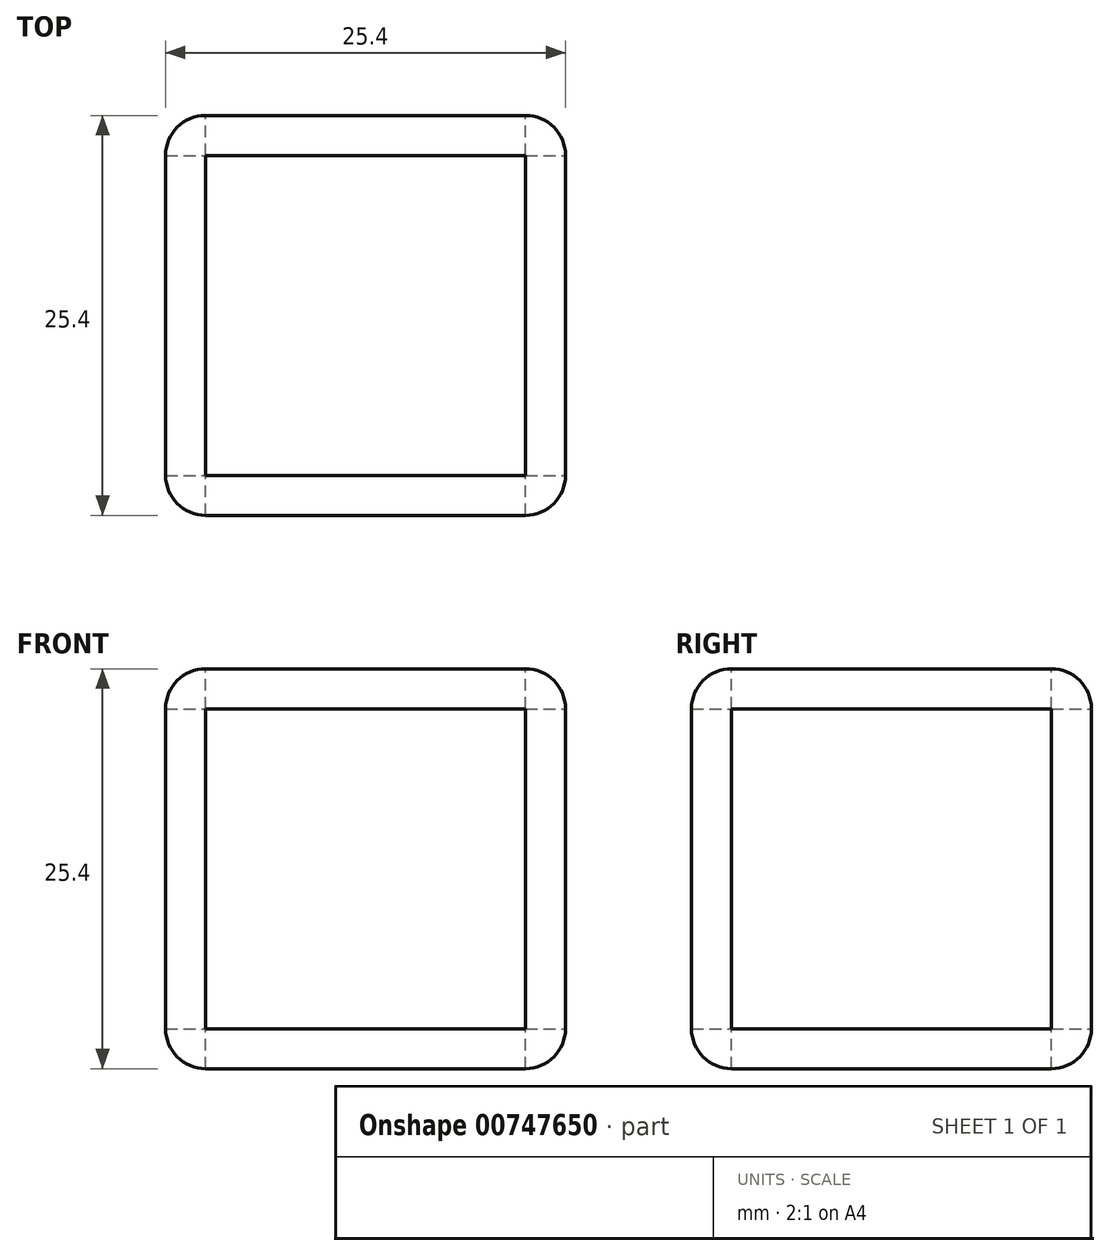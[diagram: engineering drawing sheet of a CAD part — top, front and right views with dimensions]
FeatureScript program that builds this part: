
annotation { "Feature Type Name" : "Feature", "Feature Type Description" : "" }
export const myFeature = defineFeature(function(context is Context, id is Id, definition is map)
    precondition{}
    {
        {
            var Q0;
            Q0=qCreatedBy(makeId("Front.planeOp"),FACE);
            var sketch = newSketch(context, id + "F0", { "sketchPlane" : qUnion([Q0])});
            skLineSegment(sketch, "E0.bottom", {"start": v(0, 0) * mm, "end": v(25.4, 0) * mm});
            skLineSegment(sketch, "E0.top", {"start": v(0, -25.4) * mm, "end": v(25.4, -25.4) * mm});
            skLineSegment(sketch, "E0.left", {"start": v(0, 0) * mm, "end": v(0, -25.4) * mm});
            skLineSegment(sketch, "E0.right", {"start": v(25.4, 0) * mm, "end": v(25.4, -25.4) * mm});
            skSolve(sketch);
        }
        {
            var Q0;
            Q0 = qSketchRegion(id + "F0", true);
            extrude(context, id + "F1", {"entities" : qUnion([Q0]), "depth" : 25.4 * mm, "offsetDistance" : 25.4 * mm});
        }
        {
            var Q0;
            Q0=makeQuery(id+"F1.opExtrude","CAP_EDGE",EDGE,{"disambiguationData":[OSD([sQuery(id+"F0.wireOp",EDGE,"E0.left")])],"isStart":true});
            var Q1;
            Q1=makeQuery(id+"F1.opExtrude","CAP_EDGE",EDGE,{"disambiguationData":[OSD([sQuery(id+"F0.wireOp",EDGE,"E0.left")])],"isStart":false});
            var Q2;
            Q2=makeQuery(id+"F1.opExtrude","SWEPT_EDGE",EDGE,{"disambiguationData":[OSD([sQuery(id+"F0.wireOp",EDGE,"E0.top"),sQuery(id+"F0.wireOp",EDGE,"E0.left")])]});
            var Q3;
            Q3=makeQuery(id+"F1.opExtrude","CAP_EDGE",EDGE,{"disambiguationData":[OSD([sQuery(id+"F0.wireOp",EDGE,"E0.top")])],"isStart":true});
            var Q4;
            Q4=makeQuery(id+"F1.opExtrude","CAP_EDGE",EDGE,{"disambiguationData":[OSD([sQuery(id+"F0.wireOp",EDGE,"E0.right")])],"isStart":true});
            var Q5;
            Q5=makeQuery(id+"F1.opExtrude","CAP_EDGE",EDGE,{"disambiguationData":[OSD([sQuery(id+"F0.wireOp",EDGE,"E0.bottom")])],"isStart":true});
            var Q6;
            Q6=makeQuery(id+"F1.opExtrude","SWEPT_EDGE",EDGE,{"disambiguationData":[OSD([sQuery(id+"F0.wireOp",EDGE,"E0.bottom"),sQuery(id+"F0.wireOp",EDGE,"E0.left")])]});
            var Q7;
            Q7=makeQuery(id+"F1.opExtrude","SWEPT_EDGE",EDGE,{"disambiguationData":[OSD([sQuery(id+"F0.wireOp",EDGE,"E0.bottom"),sQuery(id+"F0.wireOp",EDGE,"E0.right")])]});
            var Q8;
            Q8=makeQuery(id+"F1.opExtrude","SWEPT_EDGE",EDGE,{"disambiguationData":[OSD([sQuery(id+"F0.wireOp",EDGE,"E0.top"),sQuery(id+"F0.wireOp",EDGE,"E0.right")])]});
            var Q9;
            Q9=makeQuery(id+"F1.opExtrude","CAP_EDGE",EDGE,{"disambiguationData":[OSD([sQuery(id+"F0.wireOp",EDGE,"E0.right")])],"isStart":false});
            var Q10;
            Q10=makeQuery(id+"F1.opExtrude","CAP_EDGE",EDGE,{"disambiguationData":[OSD([sQuery(id+"F0.wireOp",EDGE,"E0.bottom")])],"isStart":false});
            fillet(context, id + "F2", {"entities" : qUnion([Q0, Q1, Q2, Q3, Q4, Q5, Q6, Q7, Q8, Q9, Q10]), "radius" : 2.54 * mm, "tangentPropagation" : true, "allowEdgeOverflow" : false});
        }
        {
            var Q0;
            Q0=makeQuery(id+"F1.opExtrude","CAP_EDGE",EDGE,{"disambiguationData":[OSD([sQuery(id+"F0.wireOp",EDGE,"E0.top")])],"isStart":false});
            fillet(context, id + "F3", {"entities" : qUnion([Q0]), "radius" : 2.54 * mm, "tangentPropagation" : true, "allowEdgeOverflow" : false});
        }
        {
            var Q0;
            Q0=makeQuery(id+"F1.opExtrude","SWEPT_FACE",FACE,{"disambiguationData":[OSD([sQuery(id+"F0.wireOp",EDGE,"E0.bottom")])]});
            extrude(context, id + "F4", {"entities" : qUnion([Q0]), "operationType" : NewBodyOperationType.REMOVE, "endBound" : BoundingType.THROUGH_ALL, "oppositeDirection" : true, "depth" : 25.4 * mm, "offsetDistance" : 25.4 * mm});
        }
        {
            var Q0;
            Q0=makeQuery(id+"F1.opExtrude","SWEPT_FACE",FACE,{"disambiguationData":[OSD([sQuery(id+"F0.wireOp",EDGE,"E0.right")])]});
            extrude(context, id + "F5", {"entities" : qUnion([Q0]), "operationType" : NewBodyOperationType.REMOVE, "endBound" : BoundingType.THROUGH_ALL, "oppositeDirection" : true, "depth" : 25.4 * mm, "offsetDistance" : 25.4 * mm});
        }
        {
            var Q0;
            Q0=makeQuery(id+"F1.opExtrude","CAP_FACE",FACE,{"disambiguationData":[OSD([sQuery(id+"F0.wireOp",EDGE,"E0.bottom"),sQuery(id+"F0.wireOp",EDGE,"E0.top"),sQuery(id+"F0.wireOp",EDGE,"E0.left"),sQuery(id+"F0.wireOp",EDGE,"E0.right")])],"isStart":true});
            extrude(context, id + "F6", {"entities" : qUnion([Q0]), "operationType" : NewBodyOperationType.REMOVE, "endBound" : BoundingType.THROUGH_ALL, "oppositeDirection" : true, "depth" : 25.4 * mm, "offsetDistance" : 25.4 * mm});
        }
    });
